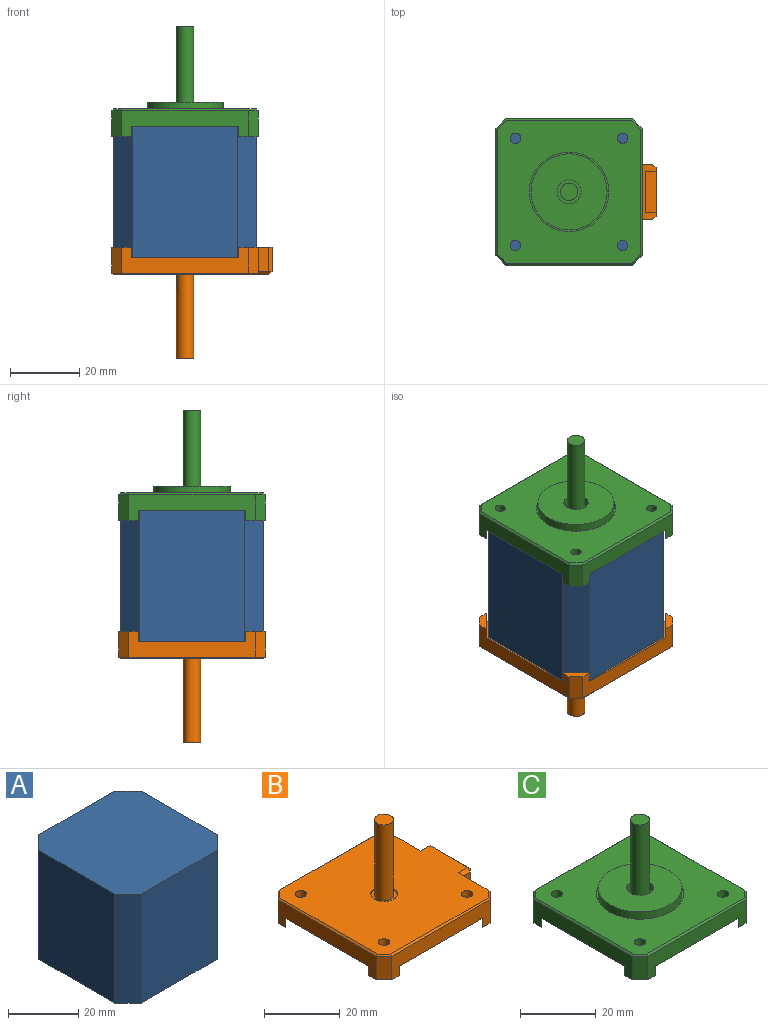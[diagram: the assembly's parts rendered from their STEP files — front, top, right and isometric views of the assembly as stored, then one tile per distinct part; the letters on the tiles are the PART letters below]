
ASSEMBLY  parts=3 mates=2
PART A: 10 faces, bbox 41.3x41.3x38 mm
  f0: plane 38x30.57mm, normal (0,1,0), area 1161.7mm2, adj f1,f7,f8,f9
  f1: plane 38x5.36mm, normal (-0.71,0.71,0), area 288.3mm2, adj f0,f2,f8,f9
  f2: plane 38x30.57mm, normal (-1,0,0), area 1161.7mm2, adj f1,f3,f8,f9
  f3: plane 38x5.36mm, normal (-0.71,-0.71,0), area 288.3mm2, adj f2,f4,f8,f9
  f4: plane 38x30.57mm, normal (0,-1,0), area 1161.7mm2, adj f3,f5,f8,f9
  f5: plane 38x5.36mm, normal (0.71,-0.71,0), area 288.3mm2, adj f4,f6,f8,f9
  f6: plane 38x30.57mm, normal (1,0,0), area 1161.7mm2, adj f5,f7,f8,f9
  f7: plane 38x5.36mm, normal (0.71,0.71,0), area 288.3mm2, adj f0,f6,f8,f9
  f8: plane 41.3x41.3mm, normal (0,0,1), area 1648.1mm2, adj f0,f1,f2,f3,f4,f5,f6,f7
  f9: plane 41.3x41.3mm, normal (0,0,-1), area 1648.1mm2, adj f0,f1,f2,f3,f4,f5,f6,f7
PART B: 52 faces, bbox 46.3x42.3x32 mm
  f0: plane 42.3x42.3mm, normal (0,0,-1), area 1697mm2, adj f1,f5,f7,f9,f11,f12,f13,f14
  f1: plane 10.82x7.5mm, normal (1,0,0), area 55.1mm2, adj f0,f2,f15,f29,f30,f35,f51
  f2: plane 7x3mm, normal (0,-1,0), area 21mm2, adj f1,f25,f28,f35,f38
  f3: plane 14x7mm, normal (1,0,0), area 38mm2, adj f24,f26,f28,f31,f33,f36,f38
  f4: plane 7x3mm, normal (0,1,0), area 21mm2, adj f5,f25,f28,f32,f33
  f5: plane 10.82x7.5mm, normal (1,0,0), area 55.1mm2, adj f0,f4,f6,f22,f23,f32,f43
  f6: plane 7.5x2.83mm, normal (0.71,0.71,0), area 30mm2, adj f5,f7,f23,f44
  f7: plane 36.64x7.5mm, normal (0,1,0), area 181.9mm2, adj f0,f6,f8,f20,f21,f22,f23,f45
  f8: plane 7.5x2.83mm, normal (-0.71,0.71,0), area 30mm2, adj f7,f9,f21,f46
  f9: plane 36.64x7.5mm, normal (-1,0,0), area 181.9mm2, adj f0,f8,f10,f18,f19,f20,f21,f47
  f10: plane 7.5x2.83mm, normal (-0.71,-0.71,0), area 30mm2, adj f9,f11,f19,f48
  f11: plane 36.64x7.5mm, normal (0,-1,0), area 181.9mm2, adj f0,f10,f15,f18,f19,f29,f30,f49
  f12: cylinder r=1.5mm len=5mm, axis (0,0,-1), area 47.1mm2, adj f0,f17
  f13: cylinder r=1.5mm len=5mm, axis (0,0,-1), area 47.1mm2, adj f0,f17
  f14: cylinder r=1.5mm len=5mm, axis (0,0,-1), area 47.1mm2, adj f0,f17
  f15: plane 7.5x2.83mm, normal (0.71,-0.71,0), area 30mm2, adj f1,f11,f30,f50
  f16: cylinder r=1.5mm len=5mm, axis (0,0,-1), area 47.1mm2, adj f0,f17
  f17: plane 44.8x41.3mm, normal (0,0,1), area 1675.1mm2, adj f12,f13,f14,f16,f32,f35,f36,f40
  f18: plane 5.66x5.66mm, normal (0.71,0.71,0), area 24mm2, adj f0,f9,f11,f19
  f19: plane 5.66x5.66mm, normal (0,0,-1), area 12mm2, adj f9,f10,f11,f18
  f20: plane 5.66x5.66mm, normal (0.71,-0.71,0), area 24mm2, adj f0,f7,f9,f21
  f21: plane 5.66x5.66mm, normal (0,0,-1), area 12mm2, adj f7,f8,f9,f20
  f22: plane 5.66x5.66mm, normal (-0.71,-0.71,0), area 24mm2, adj f0,f5,f7,f23
  f23: plane 5.66x5.66mm, normal (0,0,-1), area 12mm2, adj f5,f6,f7,f22
  f24: plane 5x3mm, normal (0,-1,0), area 15mm2, adj f3,f27,f28,f31
  f25: plane 16x3mm, normal (-1,0,0), area 48mm2, adj f0,f2,f4,f28
  f26: plane 5x3mm, normal (0,1,0), area 15mm2, adj f3,f27,f28,f31
  f27: plane 12x5mm, normal (1,0,0), area 60mm2, adj f24,f26,f28,f31
  f28: plane 16x4mm, normal (0,0,-1), area 27mm2, adj f2,f3,f4,f24,f25,f26,f27,f33
  f29: plane 5.66x5.66mm, normal (-0.71,0.71,0), area 24mm2, adj f0,f1,f11,f30
  f30: plane 5.66x5.66mm, normal (0,0,-1), area 12mm2, adj f1,f11,f15,f29
  f31: plane 12x3mm, normal (0,0,-1), area 36mm2, adj f3,f24,f26,f27
  f32: plane 3.5x1mm, normal (0,0.71,0.71), area 4.4mm2, adj f4,f5,f17,f34,f43
  f33: plane 7x1mm, normal (0.71,0.71,0), area 9.9mm2, adj f3,f4,f28,f34
  f34: plane 1x1mm, normal (0.58,0.58,0.58), area 0.9mm2, adj f32,f33,f36
  f35: plane 3.5x1mm, normal (0,-0.71,0.71), area 4.4mm2, adj f1,f2,f17,f37,f51
  f36: plane 14x1mm, normal (0.71,0,0.71), area 19.8mm2, adj f3,f17,f34,f37
  f37: plane 1x1mm, normal (0.58,-0.58,0.58), area 0.9mm2, adj f35,f36,f38
  f38: plane 7x1mm, normal (0.71,-0.71,0), area 9.9mm2, adj f2,f3,f28,f37
  f39: cylinder r=2.5mm len=24.5mm, axis (0,0,-1), area 384.8mm2, adj f41,f42
  f40: cylinder r=3.5mm len=7mm, axis (0,0,-1), area 11mm2, adj f17,f41
  f41: plane 7x7mm, normal (0,0,1), area 18.8mm2, adj f39,f40
  f42: plane 5x5mm, normal (0,0,1), area 19.6mm2, adj f39
  f43: plane 11.32x0.5mm, normal (0.71,0,0.71), area 7.8mm2, adj f5,f17,f32,f44
  f44: plane 3.04x3.04mm, normal (0.5,0.5,0.71), area 2.7mm2, adj f6,f17,f43,f45
  f45: plane 36.64x0.5mm, normal (0,0.71,0.71), area 25.8mm2, adj f7,f17,f44,f46
  f46: plane 3.04x3.04mm, normal (-0.5,0.5,0.71), area 2.7mm2, adj f8,f17,f45,f47
  f47: plane 36.64x0.5mm, normal (-0.71,0,0.71), area 25.8mm2, adj f9,f17,f46,f48
  f48: plane 3.04x3.04mm, normal (-0.5,-0.5,0.71), area 2.7mm2, adj f10,f17,f47,f49
  f49: plane 36.64x0.5mm, normal (0,-0.71,0.71), area 25.8mm2, adj f11,f17,f48,f50
  f50: plane 3.04x3.04mm, normal (0.5,-0.5,0.71), area 2.7mm2, adj f15,f17,f49,f51
  f51: plane 11.32x0.5mm, normal (0.71,0,0.71), area 7.8mm2, adj f1,f17,f35,f50
PART C: 38 faces, bbox 42.3x42.3x32 mm
  f0: plane 36.64x7.5mm, normal (-1,0,0), area 181.9mm2, adj f1,f10,f13,f14,f15,f20,f21,f32
  f1: plane 7.5x2.83mm, normal (-0.71,-0.71,0), area 30mm2, adj f0,f2,f15,f34
  f2: plane 36.64x7.5mm, normal (0,-1,0), area 181.9mm2, adj f1,f3,f13,f14,f15,f16,f17,f36
  f3: plane 7.5x2.83mm, normal (0.71,-0.71,0), area 30mm2, adj f2,f4,f17,f37
  f4: plane 36.64x7.5mm, normal (1,0,0), area 181.9mm2, adj f3,f5,f13,f16,f17,f18,f19,f35
  f5: plane 7.5x2.83mm, normal (0.71,0.71,0), area 30mm2, adj f4,f6,f19,f33
  f6: plane 36.64x7.5mm, normal (0,1,0), area 181.9mm2, adj f5,f10,f13,f18,f19,f20,f21,f31
  f7: cylinder r=1.5mm len=5mm, axis (0,0,-1), area 47.1mm2, adj f12,f13
  f8: cylinder r=1.5mm len=5mm, axis (0,0,-1), area 47.1mm2, adj f12,f13
  f9: cylinder r=1.5mm len=5mm, axis (0,0,-1), area 47.1mm2, adj f12,f13
  f10: plane 7.5x2.83mm, normal (-0.71,0.71,0), area 30mm2, adj f0,f6,f21,f30
  f11: cylinder r=1.5mm len=5mm, axis (0,0,-1), area 47.1mm2, adj f12,f13
  f12: plane 41.3x41.3mm, normal (0,0,1), area 1249.1mm2, adj f7,f8,f9,f11,f23,f30,f31,f32
  f13: plane 42.3x42.3mm, normal (0,0,-1), area 1697mm2, adj f0,f2,f4,f6,f7,f8,f9,f11
  f14: plane 5.66x5.66mm, normal (0.71,0.71,0), area 24mm2, adj f0,f2,f13,f15
  f15: plane 5.66x5.66mm, normal (0,0,-1), area 12mm2, adj f0,f1,f2,f14
  f16: plane 5.66x5.66mm, normal (-0.71,0.71,0), area 24mm2, adj f2,f4,f13,f17
  f17: plane 5.66x5.66mm, normal (0,0,-1), area 12mm2, adj f2,f3,f4,f16
  f18: plane 5.66x5.66mm, normal (-0.71,-0.71,0), area 24mm2, adj f4,f6,f13,f19
  f19: plane 5.66x5.66mm, normal (0,0,-1), area 12mm2, adj f4,f5,f6,f18
  f20: plane 5.66x5.66mm, normal (0.71,-0.71,0), area 24mm2, adj f0,f6,f13,f21
  f21: plane 5.66x5.66mm, normal (0,0,-1), area 12mm2, adj f0,f6,f10,f20
  f22: cylinder r=11mm len=22mm, axis (0,0,-1), area 172.8mm2, adj f24,f25
  f23: cylinder r=11.5mm len=23mm, axis (0,0,-1), area 36.1mm2, adj f12,f24
  f24: plane 23x23mm, normal (0,0,1), area 35.3mm2, adj f22,f23
  f25: plane 22x22mm, normal (0,0,1), area 341.6mm2, adj f22,f27
  f26: cylinder r=2.5mm len=24.5mm, axis (0,0,-1), area 384.8mm2, adj f28,f29
  f27: cylinder r=3.5mm len=7mm, axis (0,0,-1), area 55mm2, adj f25,f28
  f28: plane 7x7mm, normal (0,0,1), area 18.8mm2, adj f26,f27
  f29: plane 5x5mm, normal (0,0,1), area 19.6mm2, adj f26
  f30: plane 3.04x3.04mm, normal (-0.5,0.5,0.71), area 2.7mm2, adj f10,f12,f31,f32
  f31: plane 36.64x0.5mm, normal (0,0.71,0.71), area 25.8mm2, adj f6,f12,f30,f33
  f32: plane 36.64x0.5mm, normal (-0.71,0,0.71), area 25.8mm2, adj f0,f12,f30,f34
  f33: plane 3.04x3.04mm, normal (0.5,0.5,0.71), area 2.7mm2, adj f5,f12,f31,f35
  f34: plane 3.04x3.04mm, normal (-0.5,-0.5,0.71), area 2.7mm2, adj f1,f12,f32,f36
  f35: plane 36.64x0.5mm, normal (0.71,0,0.71), area 25.8mm2, adj f4,f12,f33,f37
  f36: plane 36.64x0.5mm, normal (0,-0.71,0.71), area 25.8mm2, adj f2,f12,f34,f37
  f37: plane 3.04x3.04mm, normal (0.5,-0.5,0.71), area 2.7mm2, adj f3,f12,f35,f36
PLACE A t=(-62.3,-126.9,-38)mm
PLACE B rot(axis=(1,0,0),180deg) t=(0,52.3,-38)mm
PLACE C at identity fixed
MATE fastened B.f39 <-> A.f9  axis (0,0,1) through (0,0,-38)mm
MATE fastened C.f23 <-> A.f8  axis (0,0,-1) through (0,0,0)mm
